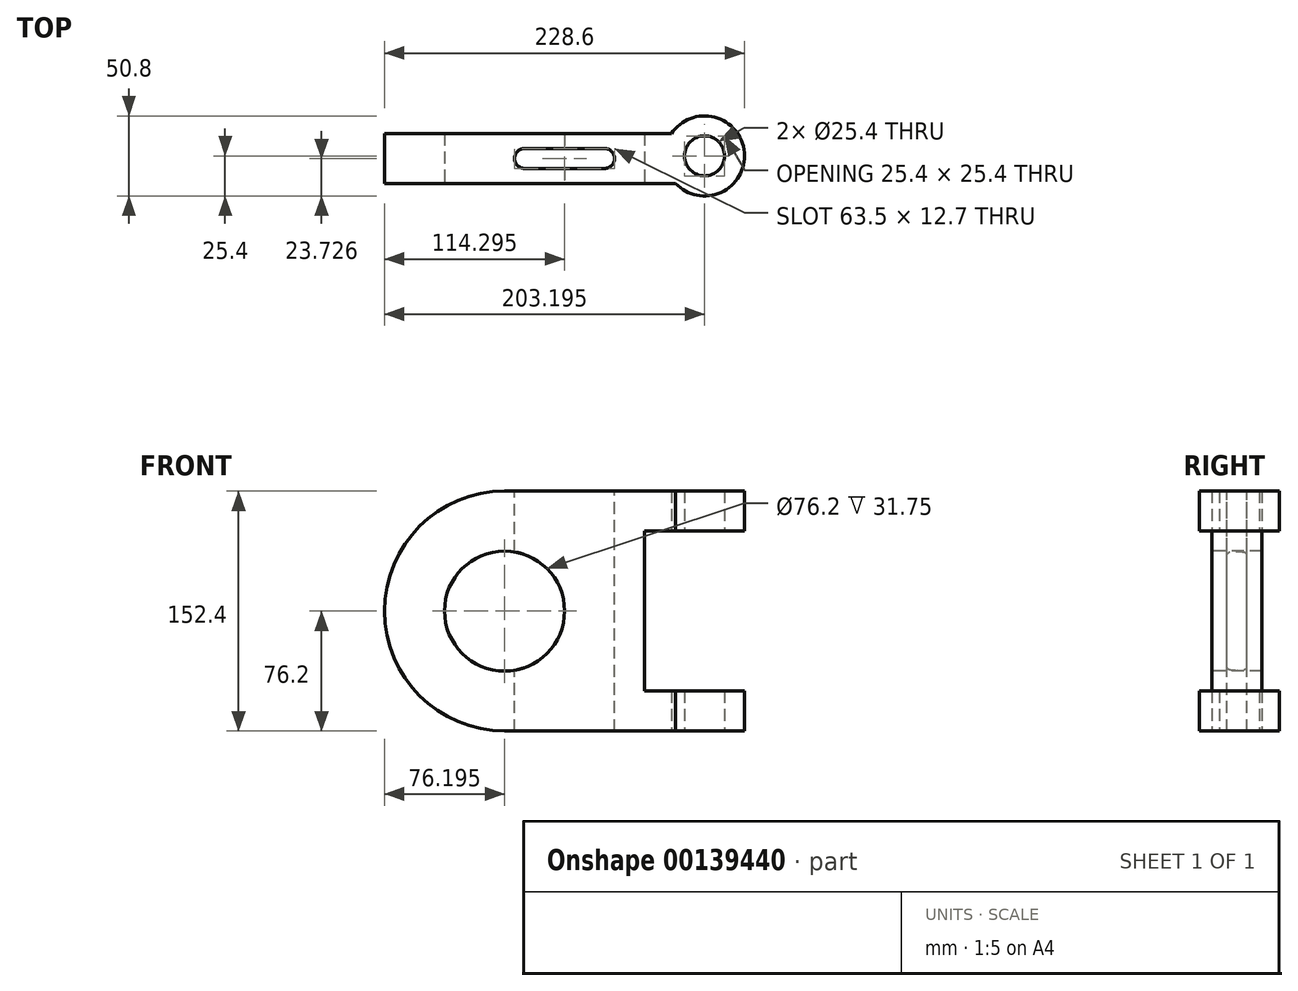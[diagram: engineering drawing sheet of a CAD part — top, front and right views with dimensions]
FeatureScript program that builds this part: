
annotation { "Feature Type Name" : "Feature", "Feature Type Description" : "" }
export const myFeature = defineFeature(function(context is Context, id is Id, definition is map)
    precondition{}
    {
        {
            var Q0;
            Q0=qCreatedBy(makeId("Top.planeOp"),FACE);
            var sketch = newSketch(context, id + "F0", { "sketchPlane" : qUnion([Q0])});
            skCircle(sketch, "E0", {"center": v(106.28, 0) * mm, "radius": 12.7 * mm});
            skCircle(sketch, "E1", {"center": v(106.28, 0) * mm, "radius": 25.4 * mm});
            skLineSegment(sketch, "E2", {"start": v(85.22, 14.2) * mm, "end": v(-96.92, 14.2) * mm});
            skLineSegment(sketch, "E3", {"start": v(87.91, -17.55) * mm, "end": v(-96.92, -17.55) * mm});
            skLineSegment(sketch, "E4", {"start": v(-96.92, 14.2) * mm, "end": v(-96.92, -17.55) * mm});
            skSolve(sketch);
        }
        {
            var Q0;
            Q0 = qSketchRegion(id + "F0", true);
            extrude(context, id + "F1", {"entities" : qUnion([Q0]), "depth" : 152.4 * mm});
        }
        {
            var Q0;
            Q0=makeQuery(id+"F1.opExtrude","SWEPT_FACE",FACE,{"disambiguationData":[OSD([sQuery(id+"F0.wireOp",EDGE,"E3")])]});
            var sketch = newSketch(context, id + "F2", { "sketchPlane" : qUnion([Q0])});
            skArc(sketch, "E5", {"start": v(-20.72, 152.4) * mm, "mid": v(-96.92, 76.2) * mm, "end": v(-20.72, 0) * mm});
            skLineSegment(sketch, "E6", {"start": v(-20.72, 152.4) * mm, "end": v(144.67, 152.4) * mm});
            skLineSegment(sketch, "E7", {"start": v(144.67, 152.4) * mm, "end": v(144.67, 0) * mm});
            skLineSegment(sketch, "E8", {"start": v(144.67, 0) * mm, "end": v(-20.72, 0) * mm});
            skCircle(sketch, "E9", {"center": v(-20.72, 76.2) * mm, "radius": 38.1 * mm});
            skLineSegment(sketch, "E10", {"start": v(-20.72, 0) * mm, "end": v(-108.67, 0) * mm});
            skLineSegment(sketch, "E11", {"start": v(-108.67, 0) * mm, "end": v(-108.67, 152.4) * mm});
            skLineSegment(sketch, "E12", {"start": v(-108.67, 152.4) * mm, "end": v(-20.72, 152.4) * mm});
            skSolve(sketch);
        }
        {
            var Q0;
            {var subQ0=sQuery(id+"F2.wireOp",EDGE,"E12");var subQ1=sQuery(id+"F2.wireOp",EDGE,"E5");var subQ2=makeQuery(id+"F2.imprint","INTERSECT",VERTEX,{"derivedFrom":[subQ1,sQuery(id+"F2.wireOp",EDGE,"E6"),subQ0]});Q0=makeQuery(id+"F2.imprint","IMPRINT",FACE,{"disambiguationData":[TD([[makeQuery(id+"F2.imprint","IMPRINT",EDGE,{"disambiguationData":[TD([[subQ2,-1.0]])],"derivedFrom":subQ1}),-1.0]])]});}
            var Q1;
            {var subQ0=sQuery(id+"F2.wireOp",EDGE,"E10");var subQ1=sQuery(id+"F2.wireOp",EDGE,"E5");var subQ2=makeQuery(id+"F2.imprint","INTERSECT",VERTEX,{"derivedFrom":[subQ1,sQuery(id+"F2.wireOp",EDGE,"E8"),subQ0]});Q1=makeQuery(id+"F2.imprint","IMPRINT",FACE,{"disambiguationData":[TD([[makeQuery(id+"F2.imprint","IMPRINT",EDGE,{"disambiguationData":[TD([[subQ2,1.0]])],"derivedFrom":subQ1}),-1.0]])]});}
            var Q2;
            {var subQ6=sQuery(id+"F2.wireOp",EDGE,"E11");Q2=makeQuery(id+"F2.imprint","IMPRINT",FACE,{"disambiguationData":[TD([[makeQuery(id+"F2.imprint","IMPRINT",EDGE,{"derivedFrom":subQ6}),-1.0]])]});}
            var Q3;
            Q3=makeQuery(id+"F2.imprint","IMPRINT",FACE,{"disambiguationData":[TD([[makeQuery(id+"F2.imprint","IMPRINT",EDGE,{"derivedFrom":sQuery(id+"F2.wireOp",EDGE,"E9")}),1.0]])]});
            extrude(context, id + "F3", {"entities" : qUnion([Q0, Q1, Q2, Q3]), "operationType" : NewBodyOperationType.REMOVE, "endBound" : BoundingType.THROUGH_ALL, "oppositeDirection" : true, "depth" : 25.4 * mm});
        }
        {
            var Q0;
            Q0=makeQuery(id+"F1.opExtrude","CAP_FACE",FACE,{"disambiguationData":[OSD([sQuery(id+"F0.wireOp",EDGE,"E0"),sQuery(id+"F0.wireOp",EDGE,"E1"),sQuery(id+"F0.wireOp",EDGE,"E2"),sQuery(id+"F0.wireOp",EDGE,"E3"),sQuery(id+"F0.wireOp",EDGE,"E4")])],"isStart":false});
            var sketch = newSketch(context, id + "F4", { "sketchPlane" : qUnion([Q0])});
            skArc(sketch, "E13", {"start": v(42.78, -8.02) * mm, "mid": v(49.13, -1.67) * mm, "end": v(42.78, 4.68) * mm});
            skArc(sketch, "E14", {"start": v(-8.02, 4.68) * mm, "mid": v(-14.37, -1.67) * mm, "end": v(-8.02, -8.02) * mm});
            skLineSegment(sketch, "E15", {"start": v(-8.02, 4.68) * mm, "end": v(42.78, 4.68) * mm});
            skLineSegment(sketch, "E16", {"start": v(-8.02, -8.02) * mm, "end": v(42.78, -8.02) * mm});
            skLineSegment(sketch, "E17", {"start": v(106.28, 25.4) * mm, "end": v(106.28, -25.4) * mm});
            skSolve(sketch);
        }
        {
            var Q0;
            Q0=makeQuery(id+"F4.imprint","IMPRINT",FACE,{"disambiguationData":[TD([[makeQuery(id+"F4.imprint","IMPRINT",EDGE,{"derivedFrom":sQuery(id+"F4.wireOp",EDGE,"E13")}),1.0]])]});
            extrude(context, id + "F5", {"entities" : qUnion([Q0]), "operationType" : NewBodyOperationType.REMOVE, "endBound" : BoundingType.THROUGH_ALL, "oppositeDirection" : true, "depth" : 25.4 * mm});
        }
        {
            var Q0;
            Q0=makeQuery(id+"F1.opExtrude","SWEPT_FACE",FACE,{"disambiguationData":[OSD([sQuery(id+"F0.wireOp",EDGE,"E3")])]});
            var sketch = newSketch(context, id + "F6", { "sketchPlane" : qUnion([Q0])});
            skLineSegment(sketch, "E18.bottom", {"start": v(68.18, 127) * mm, "end": v(225.85, 127) * mm});
            skLineSegment(sketch, "E18.top", {"start": v(68.18, 25.4) * mm, "end": v(225.85, 25.4) * mm});
            skLineSegment(sketch, "E18.left", {"start": v(68.18, 127) * mm, "end": v(68.18, 25.4) * mm});
            skLineSegment(sketch, "E18.right", {"start": v(225.85, 127) * mm, "end": v(225.85, 25.4) * mm});
            skSolve(sketch);
        }
        {
            var Q0;
            Q0 = qSketchRegion(id + "F6", true);
            var Q1;
            {var subQ0=sQuery(id+"F6.wireOp",EDGE,"E18.right");Q1=makeQuery(id+"F6.imprint","IMPRINT",FACE,{"disambiguationData":[TD([[makeQuery(id+"F6.imprint","IMPRINT",EDGE,{"derivedFrom":subQ0}),-1.0]])]});}
            extrude(context, id + "F7", {"entities" : qUnion([Q0, Q1]), "operationType" : NewBodyOperationType.REMOVE, "endBound" : BoundingType.SYMMETRIC, "oppositeDirection" : true, "depth" : 1676.4 * mm});
        }
    });
